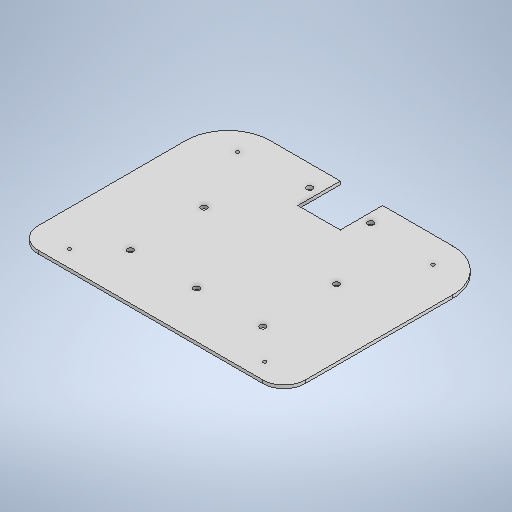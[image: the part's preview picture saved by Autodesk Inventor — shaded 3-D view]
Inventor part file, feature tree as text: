
AUTODESK INVENTOR PART (.ipt)
format: ipt  version: 2025.2 (Build 292293000, 293)  size: 294,400 bytes
history: native  units: mm
features: extrude x2, fillet x2, sketch x2
ambient origin geometry x8: Origin, YZ Plane, XZ Plane, XY Plane, X Axis, Y Axis, Z Axis, Center Point
bodies: Solid1 (feature_tree)
feature tree (6):
  extrude  "Extrusion1"  Depth=40.0mm
  fillet  "Fillet3"  Radius=10.0mm
  fillet  "Fillet4"  Radius=40.0mm
  extrude  "Extrusion2"  Depth=3.0mm
  sketch  "Sketch1"  dims[d0=252.0mm d1=47.0mm d4=10.0mm d5=40.0mm]
  sketch  "Sketch2"  dims[d6=40.0mm d7=5.5mm d8=5.5mm d9=5.5mm d10=5.5mm d11=3.0mm d12=0.0mm d15=40.0mm d16=20.0mm d17=20.0mm d18=184.34mm d19=158.6mm d20=3.0mm d21=158.6mm d22=0.0mm]
